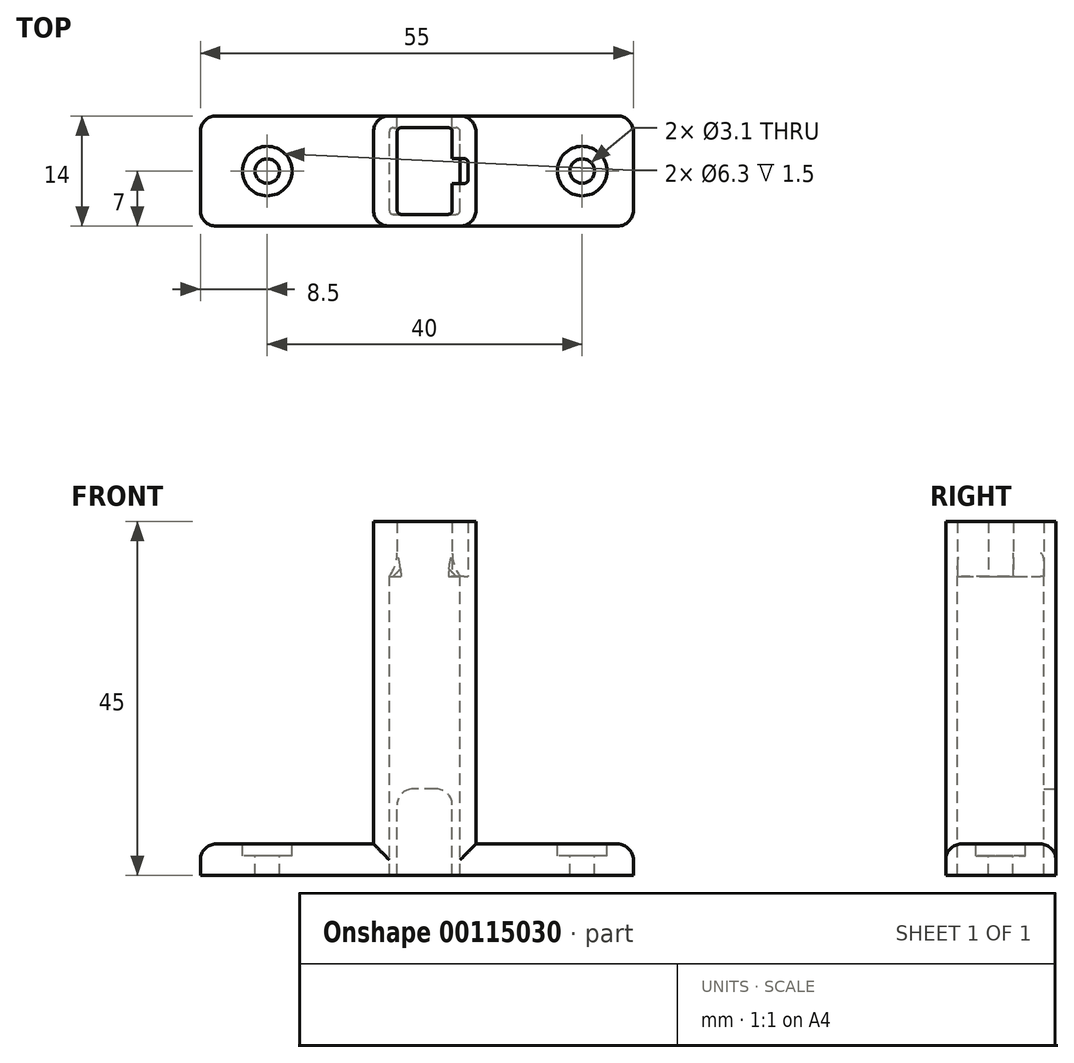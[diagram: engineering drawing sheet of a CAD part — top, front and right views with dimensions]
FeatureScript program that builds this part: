
annotation { "Feature Type Name" : "Feature", "Feature Type Description" : "" }
export const myFeature = defineFeature(function(context is Context, id is Id, definition is map)
    precondition{}
    {
        {
            var Q0;
            Q0=qCreatedBy(makeId("Top.planeOp"),FACE);
            var sketch = newSketch(context, id + "F0", { "sketchPlane" : qUnion([Q0])});
            skLineSegment(sketch, "E0", {"start": v(0, 0) * mm, "end": v(0, 11) * mm});
            skLineSegment(sketch, "E1", {"start": v(0, 11) * mm, "end": v(7, 11) * mm});
            skLineSegment(sketch, "E2", {"start": v(7, 11) * mm, "end": v(7, 7.1) * mm});
            skLineSegment(sketch, "E3", {"start": v(7, 7.1) * mm, "end": v(9, 7.1) * mm});
            skLineSegment(sketch, "E4", {"start": v(9, 7.1) * mm, "end": v(9, 3.9) * mm});
            skLineSegment(sketch, "E5", {"start": v(9, 3.9) * mm, "end": v(7, 3.9) * mm});
            skLineSegment(sketch, "E6", {"start": v(7, 3.9) * mm, "end": v(7, 0) * mm});
            skLineSegment(sketch, "E7", {"start": v(7, 0) * mm, "end": v(0, 0) * mm});
            skSolve(sketch);
        }
        {
            var Q0;
            Q0=qCreatedBy(makeId("Top.planeOp"),FACE);
            var sketch = newSketch(context, id + "F1", { "sketchPlane" : qUnion([Q0])});
            skLineSegment(sketch, "E8.bottom", {"start": v(-1, 0) * mm, "end": v(8, 0) * mm});
            skLineSegment(sketch, "E8.top", {"start": v(-1, 11) * mm, "end": v(8, 11) * mm});
            skLineSegment(sketch, "E8.left", {"start": v(-1, 0) * mm, "end": v(-1, 11) * mm});
            skLineSegment(sketch, "E8.right", {"start": v(8, 0) * mm, "end": v(8, 11) * mm});
            skSolve(sketch);
        }
        {
            var Q0;
            Q0=qCreatedBy(makeId("Top.planeOp"),FACE);
            var sketch = newSketch(context, id + "F2", { "sketchPlane" : qUnion([Q0])});
            skLineSegment(sketch, "E9.bottom", {"start": v(-3, 12.5) * mm, "end": v(10, 12.5) * mm});
            skLineSegment(sketch, "E9.top", {"start": v(-3, -1.5) * mm, "end": v(10, -1.5) * mm});
            skLineSegment(sketch, "E9.left", {"start": v(-3, 12.5) * mm, "end": v(-3, -1.5) * mm});
            skLineSegment(sketch, "E9.right", {"start": v(10, 12.5) * mm, "end": v(10, -1.5) * mm});
            skSolve(sketch);
        }
        {
            var Q0;
            Q0 = qSketchRegion(id + "F2", true);
            extrude(context, id + "F3", {"entities" : qUnion([Q0]), "depth" : 7 * mm, "hasSecondDirection" : true, "secondDirectionOppositeDirection" : true, "secondDirectionDepth" : 38 * mm});
        }
        {
            var Q0;
            Q0 = qSketchRegion(id + "F0", true);
            extrude(context, id + "F4", {"entities" : qUnion([Q0]), "depth" : 7 * mm});
        }
        {
            var Q0;
            Q0=makeQuery(id+"F3.opExtrude","SWEPT_FACE",FACE,{"disambiguationData":[OSD([sQuery(id+"F2.wireOp",EDGE,"E9.right")])]});
            var sketch = newSketch(context, id + "F5", { "sketchPlane" : qUnion([Q0])});
            skLineSegment(sketch, "E10.bottom", {"start": v(-1.5, -38) * mm, "end": v(12.5, -38) * mm});
            skLineSegment(sketch, "E10.top", {"start": v(-1.5, -34) * mm, "end": v(12.5, -34) * mm});
            skLineSegment(sketch, "E10.left", {"start": v(-1.5, -38) * mm, "end": v(-1.5, -34) * mm});
            skLineSegment(sketch, "E10.right", {"start": v(12.5, -38) * mm, "end": v(12.5, -34) * mm});
            skSolve(sketch);
        }
        {
            var Q0;
            Q0 = qSketchRegion(id + "F5", true);
            extrude(context, id + "F6", {"entities" : qUnion([Q0]), "operationType" : NewBodyOperationType.ADD, "depth" : 20 * mm, "hasSecondDirection" : true, "secondDirectionOppositeDirection" : true, "secondDirectionDepth" : 35 * mm});
        }
        {
            var Q0;
            Q0=makeQuery(id+"F4.opExtrude","SWEPT_EDGE",EDGE,{"disambiguationData":[OSD([sQuery(id+"F0.wireOp",EDGE,"E6"),sQuery(id+"F0.wireOp",EDGE,"E7")])]});
            var Q1;
            Q1=makeQuery(id+"F4.opExtrude","SWEPT_EDGE",EDGE,{"disambiguationData":[OSD([sQuery(id+"F0.wireOp",EDGE,"E1"),sQuery(id+"F0.wireOp",EDGE,"E2")])]});
            var Q2;
            Q2=makeQuery(id+"F4.opExtrude","SWEPT_EDGE",EDGE,{"disambiguationData":[OSD([sQuery(id+"F0.wireOp",EDGE,"E0"),sQuery(id+"F0.wireOp",EDGE,"E1")])]});
            var Q3;
            Q3=makeQuery(id+"F4.opExtrude","SWEPT_EDGE",EDGE,{"disambiguationData":[OSD([sQuery(id+"F0.wireOp",EDGE,"E0"),sQuery(id+"F0.wireOp",EDGE,"E7")])]});
            var Q4;
            Q4=makeQuery(id+"F4.opExtrude","SWEPT_EDGE",EDGE,{"disambiguationData":[OSD([sQuery(id+"F0.wireOp",EDGE,"E4"),sQuery(id+"F0.wireOp",EDGE,"E5")])]});
            var Q5;
            Q5=makeQuery(id+"F4.opExtrude","SWEPT_EDGE",EDGE,{"disambiguationData":[OSD([sQuery(id+"F0.wireOp",EDGE,"E3"),sQuery(id+"F0.wireOp",EDGE,"E4")])]});
            fillet(context, id + "F7", {"entities" : qUnion([Q0, Q1, Q2, Q3, Q4, Q5]), "radius" : 0.5 * mm, "tangentPropagation" : true, "allowEdgeOverflow" : false});
        }
        {
            var Q0;
            Q0 = qSketchRegion(id + "F1", true);
            var Q1;
            Q1 = qConstructionFilter(qBodyType(qCreatedBy(id + "F1" ,EDGE), BodyType.WIRE), ConstructionObject.NO);
            extrude(context, id + "F8", {"entities" : qUnion([Q0]), "surfaceEntities" : qUnion([Q1]), "oppositeDirection" : true, "depth" : 38 * mm});
        }
        {
            var Q0;
            Q0=makeQuery(id+"F8.opExtrude","SWEPT_EDGE",EDGE,{"disambiguationData":[OSD([sQuery(id+"F1.wireOp",EDGE,"E8.top"),sQuery(id+"F1.wireOp",EDGE,"E8.right")])]});
            var Q1;
            Q1=makeQuery(id+"F8.opExtrude","SWEPT_EDGE",EDGE,{"disambiguationData":[OSD([sQuery(id+"F1.wireOp",EDGE,"E8.bottom"),sQuery(id+"F1.wireOp",EDGE,"E8.right")])]});
            var Q2;
            Q2=makeQuery(id+"F8.opExtrude","SWEPT_EDGE",EDGE,{"disambiguationData":[OSD([sQuery(id+"F1.wireOp",EDGE,"E8.top"),sQuery(id+"F1.wireOp",EDGE,"E8.left")])]});
            var Q3;
            Q3=makeQuery(id+"F8.opExtrude","SWEPT_EDGE",EDGE,{"disambiguationData":[OSD([sQuery(id+"F1.wireOp",EDGE,"E8.bottom"),sQuery(id+"F1.wireOp",EDGE,"E8.left")])]});
            fillet(context, id + "F9", {"entities" : qUnion([Q0, Q1, Q2, Q3]), "radius" : 0.5 * mm, "tangentPropagation" : true, "allowEdgeOverflow" : false});
        }
        {
            var Q0;
            Q0=makeQuery(id+"F4.opExtrude","SWEPT_BODY",BODY,{"disambiguationData":[OSD([sQuery(id+"F0.wireOp",EDGE,"E0"),sQuery(id+"F0.wireOp",EDGE,"E1"),sQuery(id+"F0.wireOp",EDGE,"E2"),sQuery(id+"F0.wireOp",EDGE,"E3"),sQuery(id+"F0.wireOp",EDGE,"E4"),sQuery(id+"F0.wireOp",EDGE,"E5"),sQuery(id+"F0.wireOp",EDGE,"E6"),sQuery(id+"F0.wireOp",EDGE,"E7")])]});
            var Q1;
            Q1=makeQuery(id+"F3.opExtrude","SWEPT_BODY",BODY,{"disambiguationData":[OSD([sQuery(id+"F2.wireOp",EDGE,"E9.bottom"),sQuery(id+"F2.wireOp",EDGE,"E9.top"),sQuery(id+"F2.wireOp",EDGE,"E9.left"),sQuery(id+"F2.wireOp",EDGE,"E9.right")])]});
            booleanBodies(context, id + "F10", {"operationType" : BooleanOperationType.SUBTRACTION, "tools" : qUnion([Q0]), "targets" : qUnion([Q1])});
        }
        {
            var Q0;
            Q0=makeQuery(id+"F8.opExtrude","SWEPT_BODY",BODY,{"disambiguationData":[OSD([sQuery(id+"F1.wireOp",EDGE,"E8.bottom"),sQuery(id+"F1.wireOp",EDGE,"E8.top"),sQuery(id+"F1.wireOp",EDGE,"E8.left"),sQuery(id+"F1.wireOp",EDGE,"E8.right")])]});
            var Q1;
            Q1=makeQuery(id+"F3.opExtrude","SWEPT_BODY",BODY,{"disambiguationData":[OSD([sQuery(id+"F2.wireOp",EDGE,"E9.bottom"),sQuery(id+"F2.wireOp",EDGE,"E9.top"),sQuery(id+"F2.wireOp",EDGE,"E9.left"),sQuery(id+"F2.wireOp",EDGE,"E9.right")])]});
            booleanBodies(context, id + "F11", {"operationType" : BooleanOperationType.SUBTRACTION, "tools" : qUnion([Q0]), "targets" : qUnion([Q1])});
        }
        {
            var Q0;
            Q0=makeQuery(id+"F10.opBoolean","COPY",EDGE,{"derivedFrom":makeQuery(id+"F4.opExtrude","CAP_EDGE",EDGE,{"disambiguationData":[OSD([sQuery(id+"F0.wireOp",EDGE,"E6")])],"isStart":true})});
            var Q1;
            Q1=makeQuery(id+"F10.opBoolean","COPY",EDGE,{"derivedFrom":makeQuery(id+"F4.opExtrude","CAP_EDGE",EDGE,{"disambiguationData":[OSD([sQuery(id+"F0.wireOp",EDGE,"E2")])],"isStart":true})});
            var Q2;
            Q2=makeQuery(id+"F10.opBoolean","COPY",EDGE,{"derivedFrom":makeQuery(id+"F4.opExtrude","CAP_EDGE",EDGE,{"disambiguationData":[OSD([sQuery(id+"F0.wireOp",EDGE,"E0")])],"isStart":true})});
            fillet(context, id + "F12", {"entities" : qUnion([Q0, Q1, Q2]), "radius" : 5 * mm, "tangentPropagation" : true, "allowEdgeOverflow" : false});
        }
        {
            var Q0;
            {var subQ2=sQuery(id+"F5.wireOp",EDGE,"E10.top");Q0=makeQuery(id+"F6.boolean.opBoolean","SPLIT",FACE,{"disambiguationData":[TD([makeQuery(id+"F3.opExtrude","SWEPT_FACE",FACE,{"disambiguationData":[OSD([sQuery(id+"F2.wireOp",EDGE,"E9.right")])]})])],"derivedFrom":makeQuery(id+"F6.opExtrude","SWEPT_FACE",FACE,{"disambiguationData":[OSD([subQ2])]})});}
            var sketch = newSketch(context, id + "F13", { "sketchPlane" : qUnion([Q0])});
            skPoint(sketch, "E11", {"position": v(23.5, 5.5) * mm});
            skPoint(sketch, "E12", {"position": v(-16.5, 5.5) * mm});
            skSolve(sketch);
        }
        {
            var Q0;
            Q0=sQuery(id+"F13.wireOp",VERTEX,"E12");
            var Q1;
            Q1=sQuery(id+"F13.wireOp",VERTEX,"E11");
            var Q2;
            Q2=makeQuery(id+"F3.opExtrude","SWEPT_BODY",BODY,{"disambiguationData":[OSD([sQuery(id+"F2.wireOp",EDGE,"E9.bottom"),sQuery(id+"F2.wireOp",EDGE,"E9.top"),sQuery(id+"F2.wireOp",EDGE,"E9.left"),sQuery(id+"F2.wireOp",EDGE,"E9.right")])]});
            hole(context, id + "F14", {"style" : HoleStyle.C_BORE, "endStyle" : HoleEndStyle.BLIND, "holeDiameter" : 3.1 * mm, "cBoreDiameter" : 6.3 * mm, "cBoreDepth" : 1.5 * mm, "holeDepth" : 12 * mm, "locations" : qUnion([Q0, Q1]), "scope" : qUnion([Q2])});
        }
        {
            var Q0;
            Q0=makeQuery(id+"F6.boolean.opBoolean","MERGE",FACE,{"derivedFrom":[makeQuery(id+"F3.opExtrude","SWEPT_FACE",FACE,{"disambiguationData":[OSD([sQuery(id+"F2.wireOp",EDGE,"E9.bottom")])]}),makeQuery(id+"F6.opExtrude","SWEPT_FACE",FACE,{"disambiguationData":[OSD([sQuery(id+"F5.wireOp",EDGE,"E10.right")])]})]});
            var sketch = newSketch(context, id + "F15", { "sketchPlane" : qUnion([Q0])});
            skLineSegment(sketch, "E13.bottom", {"start": v(-7, -38) * mm, "end": v(0, -38) * mm});
            skLineSegment(sketch, "E13.top", {"start": v(-7, -27) * mm, "end": v(0, -27) * mm});
            skLineSegment(sketch, "E13.left", {"start": v(-7, -38) * mm, "end": v(-7, -27) * mm});
            skLineSegment(sketch, "E13.right", {"start": v(0, -38) * mm, "end": v(0, -27) * mm});
            skSolve(sketch);
        }
        {
            var Q0;
            Q0 = qSketchRegion(id + "F15", true);
            extrude(context, id + "F16", {"entities" : qUnion([Q0]), "operationType" : NewBodyOperationType.REMOVE, "oppositeDirection" : true, "depth" : 2 * mm});
        }
        {
            var Q0;
            Q0=makeQuery(id+"F16.boolean.opBoolean","COPY",EDGE,{"derivedFrom":makeQuery(id+"F16.opExtrude","SWEPT_EDGE",EDGE,{"disambiguationData":[OSD([sQuery(id+"F15.wireOp",EDGE,"E13.top"),sQuery(id+"F15.wireOp",EDGE,"E13.left")])]})});
            var Q1;
            Q1=makeQuery(id+"F16.boolean.opBoolean","COPY",EDGE,{"derivedFrom":makeQuery(id+"F16.opExtrude","SWEPT_EDGE",EDGE,{"disambiguationData":[OSD([sQuery(id+"F15.wireOp",EDGE,"E13.top"),sQuery(id+"F15.wireOp",EDGE,"E13.right")])]})});
            fillet(context, id + "F17", {"entities" : qUnion([Q0, Q1]), "radius" : 2 * mm, "tangentPropagation" : true, "allowEdgeOverflow" : false});
        }
        {
            var Q0;
            Q0=makeQuery(id+"F3.opExtrude","SWEPT_EDGE",EDGE,{"disambiguationData":[OSD([sQuery(id+"F2.wireOp",EDGE,"E9.bottom"),sQuery(id+"F2.wireOp",EDGE,"E9.right")])]});
            var Q1;
            Q1=makeQuery(id+"F3.opExtrude","SWEPT_EDGE",EDGE,{"disambiguationData":[OSD([sQuery(id+"F2.wireOp",EDGE,"E9.bottom"),sQuery(id+"F2.wireOp",EDGE,"E9.left")])]});
            var Q2;
            {var subQ0=sQuery(id+"F5.wireOp",EDGE,"E10.top");var subQ1=sQuery(id+"F5.wireOp",EDGE,"E10.right");var subQ2=sQuery(id+"F2.wireOp",EDGE,"E9.bottom");Q2=makeQuery(id+"F6.boolean.opBoolean","SPLIT",EDGE,{"disambiguationData":[TD([makeQuery(id+"F3.opExtrude","SWEPT_FACE",FACE,{"disambiguationData":[OSD([sQuery(id+"F2.wireOp",EDGE,"E9.left")])]})])],"derivedFrom":makeQuery(id+"F6.opExtrude","SWEPT_EDGE",EDGE,{"disambiguationData":[OSD([subQ2,sQuery(id+"F2.wireOp",EDGE,"E9.right"),subQ0,subQ1])]})});}
            var Q3;
            {var subQ0=sQuery(id+"F5.wireOp",EDGE,"E10.top");var subQ1=sQuery(id+"F5.wireOp",EDGE,"E10.right");var subQ2=sQuery(id+"F2.wireOp",EDGE,"E9.right");var subQ3=sQuery(id+"F2.wireOp",EDGE,"E9.bottom");Q3=makeQuery(id+"F6.boolean.opBoolean","SPLIT",EDGE,{"disambiguationData":[TD([makeQuery(id+"F3.opExtrude","SWEPT_FACE",FACE,{"disambiguationData":[OSD([subQ2])]})])],"derivedFrom":makeQuery(id+"F6.opExtrude","SWEPT_EDGE",EDGE,{"disambiguationData":[OSD([subQ3,subQ2,subQ0,subQ1])]})});}
            var Q4;
            {var subQ0=sQuery(id+"F5.wireOp",EDGE,"E10.top");var subQ1=sQuery(id+"F5.wireOp",EDGE,"E10.left");var subQ2=sQuery(id+"F2.wireOp",EDGE,"E9.top");Q4=makeQuery(id+"F6.boolean.opBoolean","SPLIT",EDGE,{"disambiguationData":[TD([makeQuery(id+"F3.opExtrude","SWEPT_FACE",FACE,{"disambiguationData":[OSD([sQuery(id+"F2.wireOp",EDGE,"E9.left")])]})])],"derivedFrom":makeQuery(id+"F6.opExtrude","SWEPT_EDGE",EDGE,{"disambiguationData":[OSD([subQ2,sQuery(id+"F2.wireOp",EDGE,"E9.right"),subQ0,subQ1])]})});}
            var Q5;
            {var subQ0=sQuery(id+"F5.wireOp",EDGE,"E10.top");var subQ1=sQuery(id+"F5.wireOp",EDGE,"E10.left");var subQ2=sQuery(id+"F2.wireOp",EDGE,"E9.right");var subQ3=sQuery(id+"F2.wireOp",EDGE,"E9.top");Q5=makeQuery(id+"F6.boolean.opBoolean","SPLIT",EDGE,{"disambiguationData":[TD([makeQuery(id+"F3.opExtrude","SWEPT_FACE",FACE,{"disambiguationData":[OSD([subQ2])]})])],"derivedFrom":makeQuery(id+"F6.opExtrude","SWEPT_EDGE",EDGE,{"disambiguationData":[OSD([subQ3,subQ2,subQ0,subQ1])]})});}
            var Q6;
            Q6=makeQuery(id+"F3.opExtrude","SWEPT_EDGE",EDGE,{"disambiguationData":[OSD([sQuery(id+"F2.wireOp",EDGE,"E9.top"),sQuery(id+"F2.wireOp",EDGE,"E9.left")])]});
            var Q7;
            Q7=makeQuery(id+"F3.opExtrude","SWEPT_EDGE",EDGE,{"disambiguationData":[OSD([sQuery(id+"F2.wireOp",EDGE,"E9.top"),sQuery(id+"F2.wireOp",EDGE,"E9.right")])]});
            var Q8;
            Q8=makeQuery(id+"F6.opExtrude","CAP_EDGE",EDGE,{"disambiguationData":[OSD([sQuery(id+"F5.wireOp",EDGE,"E10.left")])],"isStart":true});
            var Q9;
            Q9=makeQuery(id+"F6.opExtrude","CAP_EDGE",EDGE,{"disambiguationData":[OSD([sQuery(id+"F5.wireOp",EDGE,"E10.right")])],"isStart":true});
            var Q10;
            Q10=makeQuery(id+"F6.opExtrude","CAP_EDGE",EDGE,{"disambiguationData":[OSD([sQuery(id+"F5.wireOp",EDGE,"E10.top")])],"isStart":true});
            var Q11;
            Q11=makeQuery(id+"F6.opExtrude","CAP_EDGE",EDGE,{"disambiguationData":[OSD([sQuery(id+"F5.wireOp",EDGE,"E10.left")])],"isStart":false});
            var Q12;
            Q12=makeQuery(id+"F6.opExtrude","CAP_EDGE",EDGE,{"disambiguationData":[OSD([sQuery(id+"F5.wireOp",EDGE,"E10.top")])],"isStart":false});
            var Q13;
            Q13=makeQuery(id+"F6.opExtrude","CAP_EDGE",EDGE,{"disambiguationData":[OSD([sQuery(id+"F5.wireOp",EDGE,"E10.right")])],"isStart":false});
            fillet(context, id + "F18", {"entities" : qUnion([Q0, Q1, Q2, Q3, Q4, Q5, Q6, Q7, Q8, Q9, Q10, Q11, Q12, Q13]), "radius" : 2 * mm, "tangentPropagation" : true, "allowEdgeOverflow" : false});
        }
    });
